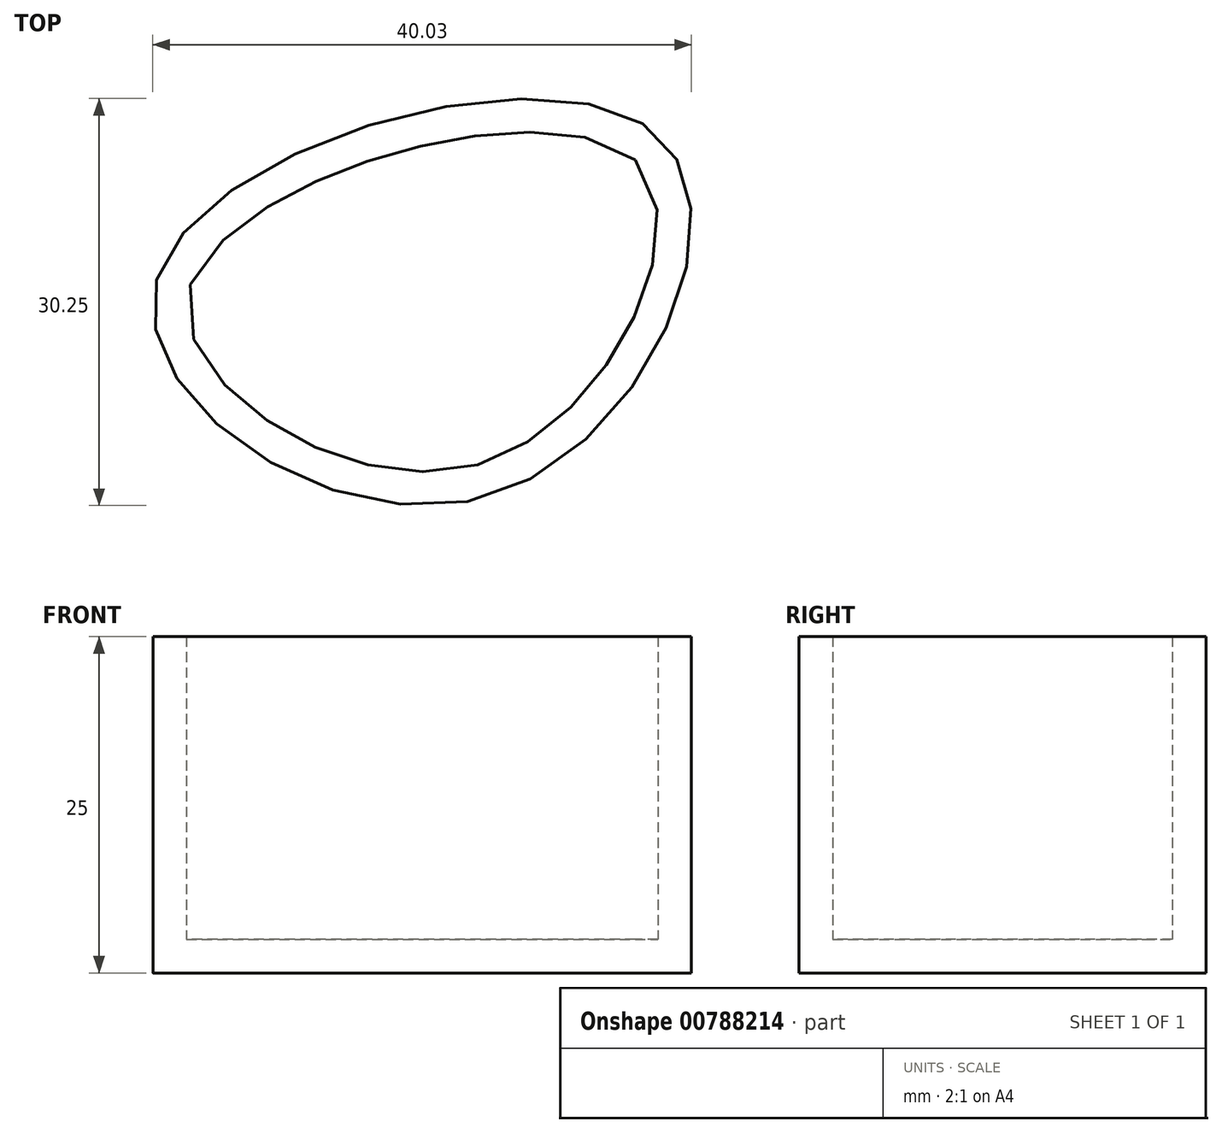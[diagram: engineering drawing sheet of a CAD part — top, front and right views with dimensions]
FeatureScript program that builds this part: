
annotation { "Feature Type Name" : "Feature", "Feature Type Description" : "" }
export const myFeature = defineFeature(function(context is Context, id is Id, definition is map)
    precondition{}
    {
        {
            var Q0;
            Q0=qCreatedBy(makeId("Top.planeOp"),FACE);
            var sketch = newSketch(context, id + "F0", { "sketchPlane" : qUnion([Q0])});
            skFitSpline(sketch, "E0", {"points": [v(-167.33, -101.45) * mm, v(-142.86, -117.6) * mm, v(-130.07, -90.69) * mm, v(-167.33, -101.45) * mm]});
            skSolve(sketch);
        }
        {
            var Q0;
            Q0 = qSketchRegion(id + "F0", true);
            extrude(context, id + "F1", {"entities" : qUnion([Q0]), "depth" : 25 * mm, "offsetDistance" : 25 * mm});
        }
        {
            var Q0;
            Q0=makeQuery(id+"F1.opExtrude","CAP_FACE",FACE,{"disambiguationData":[OSD([sQuery(id+"F0.wireOp",EDGE,"E0")])],"isStart":false});
            shell(context, id + "F2", {"entities" : qUnion([Q0]), "thickness" : 2.5 * mm});
        }
    });
